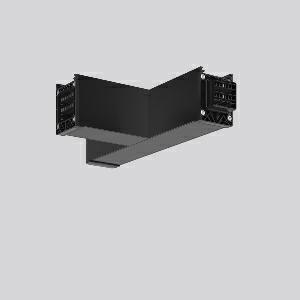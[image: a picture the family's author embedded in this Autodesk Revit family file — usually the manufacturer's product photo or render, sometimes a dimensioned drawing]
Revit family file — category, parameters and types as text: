
# Revit family: linedo_t-verbindung_982774_003_7_1822
name_source: partatom
category: Lighting Fixtures
units: mm (PartAtom-declared; Revit-internal decimal feet)

## family parameters
Cut with Voids When Loaded = No
Host = Face
Light Source = No
Part Type = Normal
Room Calculation Point = No
Round Connector Dimension = Use Diameter
Shared = No

## types (1)
- LINEDO T-Verbindung
    Apparent Load = 0 VA
    Default Elevation = 1800 mm
    Description = Series: LINEDO
T-connector, 7-pole, connection plug / socket - socket. Housing: extruded aluminium profile, powder-coated. Cover made of plastic, surface like housing. LINEDO plug system, plastic, black. Easy connection for rigid or flexible wires. 5 membrane cable entries (2 x M20 and 3 x M25). Suitable for power supply in 7-pole version. Ready prewired. Colour-coded individual cables enable easy electromechanical separation.
Colour: jet black (RAL 9005)
Length: 330 mm
Width: 185 mm
Height: 76 mm
Weight: 940 g
    Height = 76 mm
    Lamp = 0 x
    Length = 331 mm
    Luminous efficacy = 0 lm/W
    Manufacturer = RZB
    ModVariant = No
    Model = 982774.003.7
    Mounting Place = Ceiling
    Mounting Type = Surface mounted
    Number of Poles = 1
    OnlyDefault = Yes
    Power Factor = 1
    Product Name = LINEDO T-Verbindung
    Product group = Surface mounted continuous line luminaire system
    ProductGroupID = 310
    Protection Class = Protection class I
    Protection Degree = Degree of protection
    RLX_Detail_Level = 1
    RLX_Emergency_Light_Flux = 0 lm
    RLX_Emergency_Type = 0
    RLX_Emergency_Type_DB = No
    RlxData = <blob elided: 19929 chars, md5=3de548d5>
    Standby Power = 0 W
    System Light Flux = 0 lm
    System Power = 0 W
    Type Comments = Product without accessories
    Type Image = 982774.003.3.jpg
    URL = http://relux.com
    VarID = ---
    Voltage = 0 V
    Weight = 0.00 kg
    Width = 185 mm

## geometry (parser evidence)
native form markers: Blend x4, Sweep x11
no freeform markers — native parametric forms only
